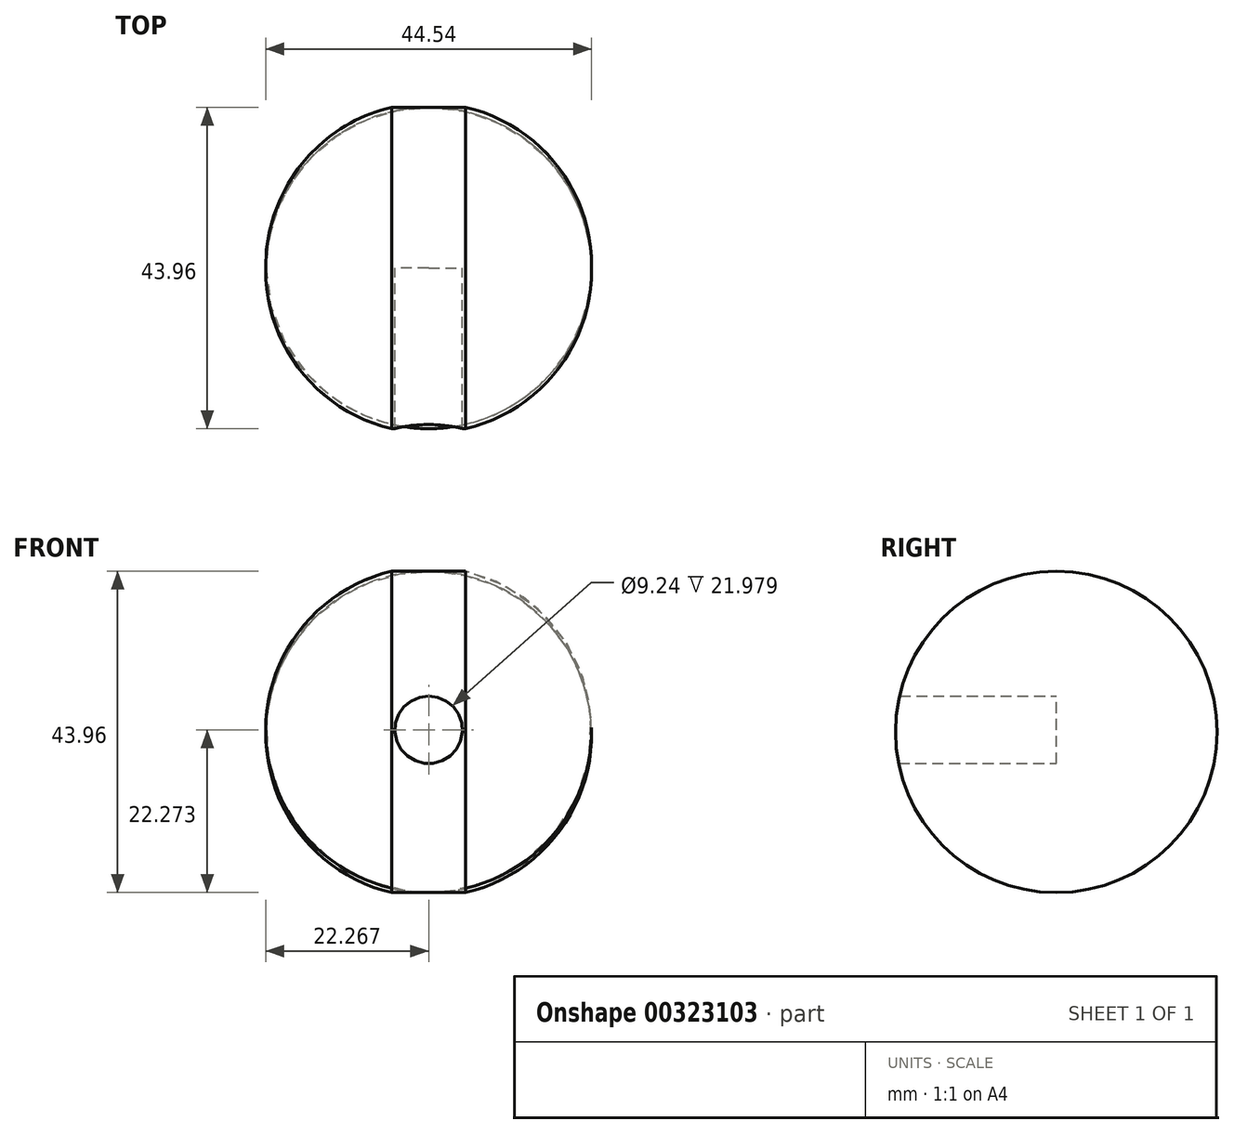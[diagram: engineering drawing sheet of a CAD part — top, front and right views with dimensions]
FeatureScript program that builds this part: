
annotation { "Feature Type Name" : "Feature", "Feature Type Description" : "" }
export const myFeature = defineFeature(function(context is Context, id is Id, definition is map)
    precondition{}
    {
        {
            var Q0;
            Q0=qCreatedBy(makeId("Front.planeOp"),FACE);
            var sketch = newSketch(context, id + "F0", { "sketchPlane" : qUnion([Q0])});
            skArc(sketch, "E0", {"start": v(44.53, 0) * mm, "mid": v(22.27, 22.56) * mm, "end": v(0, 0) * mm});
            skLineSegment(sketch, "E1", {"start": v(0, 0) * mm, "end": v(44.53, 0) * mm});
            skLineSegment(sketch, "E2", {"start": v(17.2, 0) * mm, "end": v(17.2, 21.98) * mm});
            skLineSegment(sketch, "E3", {"start": v(27.34, 0) * mm, "end": v(27.34, 21.98) * mm});
            skLineSegment(sketch, "E4", {"start": v(17.2, 21.98) * mm, "end": v(27.34, 21.98) * mm});
            skSolve(sketch);
        }
        {
            var Q0;
            Q0=makeQuery(id+"F0.imprint","IMPRINT",FACE,{"disambiguationData":[TD([[makeQuery(id+"F0.imprint","IMPRINT",EDGE,{"derivedFrom":sQuery(id+"F0.wireOp",EDGE,"E0")}),1.0]])]});
            var Q1;
            {var subQ3=sQuery(id+"F0.wireOp",EDGE,"E2");Q1=makeQuery(id+"F0.imprint","IMPRINT",FACE,{"disambiguationData":[TD([[makeQuery(id+"F0.imprint","IMPRINT",EDGE,{"derivedFrom":subQ3}),1.0]])]});}
            var Q2;
            {var subQ3=sQuery(id+"F0.wireOp",EDGE,"E3");Q2=makeQuery(id+"F0.imprint","IMPRINT",FACE,{"disambiguationData":[TD([[makeQuery(id+"F0.imprint","IMPRINT",EDGE,{"derivedFrom":subQ3}),-1.0]])]});}
            var Q3;
            Q3=sQuery(id+"F0.wireOp",EDGE,"E0");
            var Q4;
            Q4=sQuery(id+"F0.wireOp",EDGE,"E1");
            var Q5;
            Q5=sQuery(id+"F0.wireOp",EDGE,"E1");
            revolve(context, id + "F1", {"entities" : qUnion([Q0, Q1, Q2]), "surfaceEntities" : qUnion([Q3, Q4]), "axis" : qUnion([Q5]), "revolveType" : RevolveType.FULL});
        }
        {
            var Q0;
            Q0=qCreatedBy(makeId("Front.planeOp"),FACE);
            var sketch = newSketch(context, id + "F2", { "sketchPlane" : qUnion([Q0])});
            skCircle(sketch, "E5", {"center": v(22.27, 0.3) * mm, "radius": 4.62 * mm});
            skSolve(sketch);
        }
        {
            var Q0;
            Q0 = qSketchRegion(id + "F2", true);
            extrude(context, id + "F3", {"entities" : qUnion([Q0]), "operationType" : NewBodyOperationType.ADD, "depth" : 25.4 * mm});
        }
    });
